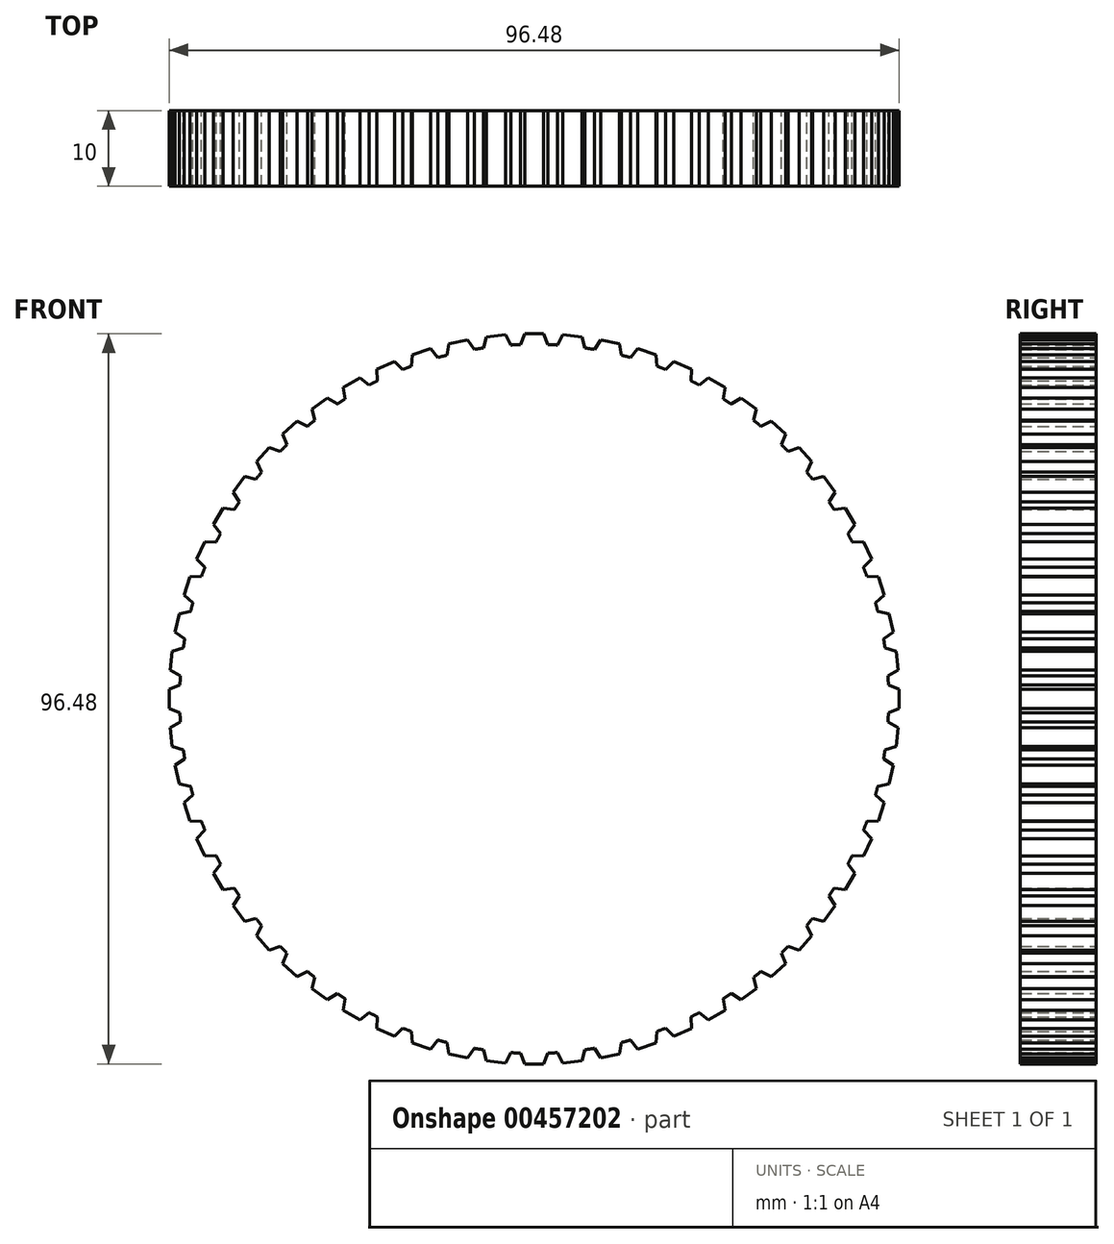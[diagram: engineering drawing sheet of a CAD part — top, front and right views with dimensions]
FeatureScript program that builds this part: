
annotation { "Feature Type Name" : "Feature", "Feature Type Description" : "" }
export const myFeature = defineFeature(function(context is Context, id is Id, definition is map)
    precondition{}
    {
        {
            var Q0;
            Q0=qCreatedBy(makeId("Front.planeOp"),FACE);
            var sketch = newSketch(context, id + "F0", { "sketchPlane" : qUnion([Q0])});
            skCircle(sketch, "E0", {"center": v(0, 0) * mm, "radius": 48.26 * mm, "construction": true});
            skLineSegment(sketch, "E1", {"start": v(0, 48.26) * mm, "end": v(0, 46.86) * mm, "construction": true});
            skCircle(sketch, "E2", {"center": v(0, 0) * mm, "radius": 46.86 * mm});
            skLineSegment(sketch, "E3", {"start": v(0, 0) * mm, "end": v(-1.26, 48.24) * mm, "construction": true});
            skLineSegment(sketch, "E4", {"start": v(0, 0) * mm, "end": v(-2.53, 48.19) * mm, "construction": true});
            skLineSegment(sketch, "E5.MirrorCS", {"start": v(0, 0) * mm, "end": v(1.26, 48.24) * mm, "construction": true});
            skLineSegment(sketch, "E6.MirrorCS", {"start": v(0, 0) * mm, "end": v(2.53, 48.19) * mm, "construction": true});
            skLineSegment(sketch, "E7", {"start": v(-1.26, 48.24) * mm, "end": v(1.26, 48.24) * mm});
            skLineSegment(sketch, "E8", {"start": v(-1.26, 48.24) * mm, "end": v(-1.84, 46.82) * mm});
            skLineSegment(sketch, "E9.MirrorCS", {"start": v(1.26, 48.24) * mm, "end": v(1.84, 46.82) * mm});
            skLineSegment(sketch, "E10.1.0", {"start": v(-6.3, 47.84) * mm, "end": v(-6.72, 46.37) * mm});
            skLineSegment(sketch, "E10.1.1", {"start": v(-6.3, 47.84) * mm, "end": v(-3.79, 48.1) * mm});
            skLineSegment(sketch, "E10.1.2", {"start": v(-3.79, 48.1) * mm, "end": v(-3.07, 46.75) * mm});
            skLineSegment(sketch, "E10.2.0", {"start": v(-11.26, 46.92) * mm, "end": v(-11.53, 45.41) * mm});
            skLineSegment(sketch, "E10.2.1", {"start": v(-11.26, 46.92) * mm, "end": v(-8.8, 47.45) * mm});
            skLineSegment(sketch, "E10.2.2", {"start": v(-8.8, 47.45) * mm, "end": v(-7.94, 46.18) * mm});
            skLineSegment(sketch, "E10.3.0", {"start": v(-16.1, 45.49) * mm, "end": v(-16.21, 43.96) * mm});
            skLineSegment(sketch, "E10.3.1", {"start": v(-16.1, 45.49) * mm, "end": v(-13.7, 46.27) * mm});
            skLineSegment(sketch, "E10.3.2", {"start": v(-13.7, 46.27) * mm, "end": v(-12.72, 45.1) * mm});
            skLineSegment(sketch, "E10.4.0", {"start": v(-20.77, 43.55) * mm, "end": v(-20.72, 42.02) * mm});
            skLineSegment(sketch, "E10.4.1", {"start": v(-20.77, 43.55) * mm, "end": v(-18.47, 44.58) * mm});
            skLineSegment(sketch, "E10.4.2", {"start": v(-18.47, 44.58) * mm, "end": v(-17.37, 43.52) * mm});
            skLineSegment(sketch, "E10.5.0", {"start": v(-25.21, 41.14) * mm, "end": v(-25, 39.63) * mm});
            skLineSegment(sketch, "E10.5.1", {"start": v(-25.21, 41.14) * mm, "end": v(-23.03, 42.4) * mm});
            skLineSegment(sketch, "E10.5.2", {"start": v(-23.03, 42.4) * mm, "end": v(-21.82, 41.46) * mm});
            skLineSegment(sketch, "E10.6.0", {"start": v(-29.38, 38.28) * mm, "end": v(-29, 36.8) * mm});
            skLineSegment(sketch, "E10.6.1", {"start": v(-29.38, 38.28) * mm, "end": v(-27.33, 39.77) * mm});
            skLineSegment(sketch, "E10.6.2", {"start": v(-27.33, 39.77) * mm, "end": v(-26.03, 38.96) * mm});
            skLineSegment(sketch, "E10.7.0", {"start": v(-33.22, 35) * mm, "end": v(-32.7, 33.56) * mm});
            skLineSegment(sketch, "E10.7.1", {"start": v(-33.22, 35) * mm, "end": v(-31.34, 36.7) * mm});
            skLineSegment(sketch, "E10.7.2", {"start": v(-31.34, 36.7) * mm, "end": v(-29.96, 36.02) * mm});
            skLineSegment(sketch, "E10.8.0", {"start": v(-36.7, 31.34) * mm, "end": v(-36.02, 29.96) * mm});
            skLineSegment(sketch, "E10.8.1", {"start": v(-36.7, 31.34) * mm, "end": v(-35, 33.22) * mm});
            skLineSegment(sketch, "E10.8.2", {"start": v(-35, 33.22) * mm, "end": v(-33.56, 32.7) * mm});
            skLineSegment(sketch, "E10.9.0", {"start": v(-39.77, 27.33) * mm, "end": v(-38.96, 26.03) * mm});
            skLineSegment(sketch, "E10.9.1", {"start": v(-39.77, 27.33) * mm, "end": v(-38.28, 29.38) * mm});
            skLineSegment(sketch, "E10.9.2", {"start": v(-38.28, 29.38) * mm, "end": v(-36.8, 29) * mm});
            skLineSegment(sketch, "E11", {"start": v(0, 0) * mm, "end": v(0, 48.26) * mm, "construction": true});
            skLineSegment(sketch, "E12.2.10.0", {"start": v(-42.4, 23.03) * mm, "end": v(-41.46, 21.82) * mm});
            skLineSegment(sketch, "E12.3.10.0", {"start": v(-42.4, 23.03) * mm, "end": v(-41.14, 25.21) * mm});
            skLineSegment(sketch, "E12.6.10.0", {"start": v(-41.14, 25.21) * mm, "end": v(-39.63, 25) * mm});
            skLineSegment(sketch, "E12.2.11.0", {"start": v(-44.58, 18.47) * mm, "end": v(-43.52, 17.37) * mm});
            skLineSegment(sketch, "E12.3.11.0", {"start": v(-44.58, 18.47) * mm, "end": v(-43.55, 20.77) * mm});
            skLineSegment(sketch, "E12.6.11.0", {"start": v(-43.55, 20.77) * mm, "end": v(-42.02, 20.72) * mm});
            skLineSegment(sketch, "E12.2.12.0", {"start": v(-46.27, 13.7) * mm, "end": v(-45.1, 12.72) * mm});
            skLineSegment(sketch, "E12.3.12.0", {"start": v(-46.27, 13.7) * mm, "end": v(-45.49, 16.1) * mm});
            skLineSegment(sketch, "E12.6.12.0", {"start": v(-45.49, 16.1) * mm, "end": v(-43.96, 16.21) * mm});
            skLineSegment(sketch, "E12.2.13.0", {"start": v(-47.45, 8.8) * mm, "end": v(-46.18, 7.94) * mm});
            skLineSegment(sketch, "E12.3.13.0", {"start": v(-47.45, 8.8) * mm, "end": v(-46.92, 11.26) * mm});
            skLineSegment(sketch, "E12.6.13.0", {"start": v(-46.92, 11.26) * mm, "end": v(-45.41, 11.53) * mm});
            skLineSegment(sketch, "E12.2.14.0", {"start": v(-48.1, 3.79) * mm, "end": v(-46.75, 3.07) * mm});
            skLineSegment(sketch, "E12.3.14.0", {"start": v(-48.1, 3.79) * mm, "end": v(-47.84, 6.3) * mm});
            skLineSegment(sketch, "E12.6.14.0", {"start": v(-47.84, 6.3) * mm, "end": v(-46.37, 6.72) * mm});
            skLineSegment(sketch, "E12.2.15.0", {"start": v(-48.24, -1.26) * mm, "end": v(-46.82, -1.84) * mm});
            skLineSegment(sketch, "E12.3.15.0", {"start": v(-48.24, -1.26) * mm, "end": v(-48.24, 1.26) * mm});
            skLineSegment(sketch, "E12.6.15.0", {"start": v(-48.24, 1.26) * mm, "end": v(-46.82, 1.84) * mm});
            skLineSegment(sketch, "E12.2.16.0", {"start": v(-47.84, -6.3) * mm, "end": v(-46.37, -6.72) * mm});
            skLineSegment(sketch, "E12.3.16.0", {"start": v(-47.84, -6.3) * mm, "end": v(-48.1, -3.79) * mm});
            skLineSegment(sketch, "E12.6.16.0", {"start": v(-48.1, -3.79) * mm, "end": v(-46.75, -3.07) * mm});
            skLineSegment(sketch, "E12.2.17.0", {"start": v(-46.92, -11.26) * mm, "end": v(-45.41, -11.53) * mm});
            skLineSegment(sketch, "E12.3.17.0", {"start": v(-46.92, -11.26) * mm, "end": v(-47.45, -8.8) * mm});
            skLineSegment(sketch, "E12.6.17.0", {"start": v(-47.45, -8.8) * mm, "end": v(-46.18, -7.94) * mm});
            skLineSegment(sketch, "E12.2.18.0", {"start": v(-45.49, -16.1) * mm, "end": v(-43.96, -16.21) * mm});
            skLineSegment(sketch, "E12.3.18.0", {"start": v(-45.49, -16.1) * mm, "end": v(-46.27, -13.7) * mm});
            skLineSegment(sketch, "E12.6.18.0", {"start": v(-46.27, -13.7) * mm, "end": v(-45.1, -12.72) * mm});
            skLineSegment(sketch, "E12.2.19.0", {"start": v(-43.55, -20.77) * mm, "end": v(-42.02, -20.72) * mm});
            skLineSegment(sketch, "E12.3.19.0", {"start": v(-43.55, -20.77) * mm, "end": v(-44.58, -18.47) * mm});
            skLineSegment(sketch, "E12.6.19.0", {"start": v(-44.58, -18.47) * mm, "end": v(-43.52, -17.37) * mm});
            skLineSegment(sketch, "E12.2.20.0", {"start": v(-41.14, -25.21) * mm, "end": v(-39.63, -25) * mm});
            skLineSegment(sketch, "E12.3.20.0", {"start": v(-41.14, -25.21) * mm, "end": v(-42.4, -23.03) * mm});
            skLineSegment(sketch, "E12.6.20.0", {"start": v(-42.4, -23.03) * mm, "end": v(-41.46, -21.82) * mm});
            skLineSegment(sketch, "E12.2.21.0", {"start": v(-38.28, -29.38) * mm, "end": v(-36.8, -29) * mm});
            skLineSegment(sketch, "E12.3.21.0", {"start": v(-38.28, -29.38) * mm, "end": v(-39.77, -27.33) * mm});
            skLineSegment(sketch, "E12.6.21.0", {"start": v(-39.77, -27.33) * mm, "end": v(-38.96, -26.03) * mm});
            skLineSegment(sketch, "E12.2.22.0", {"start": v(-35, -33.22) * mm, "end": v(-33.56, -32.7) * mm});
            skLineSegment(sketch, "E12.3.22.0", {"start": v(-35, -33.22) * mm, "end": v(-36.7, -31.34) * mm});
            skLineSegment(sketch, "E12.6.22.0", {"start": v(-36.7, -31.34) * mm, "end": v(-36.02, -29.96) * mm});
            skLineSegment(sketch, "E12.2.23.0", {"start": v(-31.34, -36.7) * mm, "end": v(-29.96, -36.02) * mm});
            skLineSegment(sketch, "E12.3.23.0", {"start": v(-31.34, -36.7) * mm, "end": v(-33.22, -35) * mm});
            skLineSegment(sketch, "E12.6.23.0", {"start": v(-33.22, -35) * mm, "end": v(-32.7, -33.56) * mm});
            skLineSegment(sketch, "E12.2.24.0", {"start": v(-27.33, -39.77) * mm, "end": v(-26.03, -38.96) * mm});
            skLineSegment(sketch, "E12.3.24.0", {"start": v(-27.33, -39.77) * mm, "end": v(-29.38, -38.28) * mm});
            skLineSegment(sketch, "E12.6.24.0", {"start": v(-29.38, -38.28) * mm, "end": v(-29, -36.8) * mm});
            skLineSegment(sketch, "E12.2.25.0", {"start": v(-23.03, -42.4) * mm, "end": v(-21.82, -41.46) * mm});
            skLineSegment(sketch, "E12.3.25.0", {"start": v(-23.03, -42.4) * mm, "end": v(-25.21, -41.14) * mm});
            skLineSegment(sketch, "E12.6.25.0", {"start": v(-25.21, -41.14) * mm, "end": v(-25, -39.63) * mm});
            skLineSegment(sketch, "E12.2.26.0", {"start": v(-18.47, -44.58) * mm, "end": v(-17.37, -43.52) * mm});
            skLineSegment(sketch, "E12.3.26.0", {"start": v(-18.47, -44.58) * mm, "end": v(-20.77, -43.55) * mm});
            skLineSegment(sketch, "E12.6.26.0", {"start": v(-20.77, -43.55) * mm, "end": v(-20.72, -42.02) * mm});
            skLineSegment(sketch, "E12.2.27.0", {"start": v(-13.7, -46.27) * mm, "end": v(-12.72, -45.1) * mm});
            skLineSegment(sketch, "E12.3.27.0", {"start": v(-13.7, -46.27) * mm, "end": v(-16.1, -45.49) * mm});
            skLineSegment(sketch, "E12.6.27.0", {"start": v(-16.1, -45.49) * mm, "end": v(-16.21, -43.96) * mm});
            skLineSegment(sketch, "E12.2.28.0", {"start": v(-8.8, -47.45) * mm, "end": v(-7.94, -46.18) * mm});
            skLineSegment(sketch, "E12.3.28.0", {"start": v(-8.8, -47.45) * mm, "end": v(-11.26, -46.92) * mm});
            skLineSegment(sketch, "E12.6.28.0", {"start": v(-11.26, -46.92) * mm, "end": v(-11.53, -45.41) * mm});
            skLineSegment(sketch, "E12.2.29.0", {"start": v(-3.79, -48.1) * mm, "end": v(-3.07, -46.75) * mm});
            skLineSegment(sketch, "E12.3.29.0", {"start": v(-3.79, -48.1) * mm, "end": v(-6.3, -47.84) * mm});
            skLineSegment(sketch, "E12.6.29.0", {"start": v(-6.3, -47.84) * mm, "end": v(-6.72, -46.37) * mm});
            skLineSegment(sketch, "E12.2.30.0", {"start": v(1.26, -48.24) * mm, "end": v(1.84, -46.82) * mm});
            skLineSegment(sketch, "E12.3.30.0", {"start": v(1.26, -48.24) * mm, "end": v(-1.26, -48.24) * mm});
            skLineSegment(sketch, "E12.6.30.0", {"start": v(-1.26, -48.24) * mm, "end": v(-1.84, -46.82) * mm});
            skLineSegment(sketch, "E12.2.31.0", {"start": v(6.3, -47.84) * mm, "end": v(6.72, -46.37) * mm});
            skLineSegment(sketch, "E12.3.31.0", {"start": v(6.3, -47.84) * mm, "end": v(3.79, -48.1) * mm});
            skLineSegment(sketch, "E12.6.31.0", {"start": v(3.79, -48.1) * mm, "end": v(3.07, -46.75) * mm});
            skLineSegment(sketch, "E12.2.32.0", {"start": v(11.26, -46.92) * mm, "end": v(11.53, -45.41) * mm});
            skLineSegment(sketch, "E12.3.32.0", {"start": v(11.26, -46.92) * mm, "end": v(8.8, -47.45) * mm});
            skLineSegment(sketch, "E12.6.32.0", {"start": v(8.8, -47.45) * mm, "end": v(7.94, -46.18) * mm});
            skLineSegment(sketch, "E12.2.33.0", {"start": v(16.1, -45.49) * mm, "end": v(16.21, -43.96) * mm});
            skLineSegment(sketch, "E12.3.33.0", {"start": v(16.1, -45.49) * mm, "end": v(13.7, -46.27) * mm});
            skLineSegment(sketch, "E12.6.33.0", {"start": v(13.7, -46.27) * mm, "end": v(12.72, -45.1) * mm});
            skLineSegment(sketch, "E12.2.34.0", {"start": v(20.77, -43.55) * mm, "end": v(20.72, -42.02) * mm});
            skLineSegment(sketch, "E12.3.34.0", {"start": v(20.77, -43.55) * mm, "end": v(18.47, -44.58) * mm});
            skLineSegment(sketch, "E12.6.34.0", {"start": v(18.47, -44.58) * mm, "end": v(17.37, -43.52) * mm});
            skLineSegment(sketch, "E12.2.35.0", {"start": v(25.21, -41.14) * mm, "end": v(25, -39.63) * mm});
            skLineSegment(sketch, "E12.3.35.0", {"start": v(25.21, -41.14) * mm, "end": v(23.03, -42.4) * mm});
            skLineSegment(sketch, "E12.6.35.0", {"start": v(23.03, -42.4) * mm, "end": v(21.82, -41.46) * mm});
            skLineSegment(sketch, "E12.2.36.0", {"start": v(29.38, -38.28) * mm, "end": v(29, -36.8) * mm});
            skLineSegment(sketch, "E12.3.36.0", {"start": v(29.38, -38.28) * mm, "end": v(27.33, -39.77) * mm});
            skLineSegment(sketch, "E12.6.36.0", {"start": v(27.33, -39.77) * mm, "end": v(26.03, -38.96) * mm});
            skLineSegment(sketch, "E12.2.37.0", {"start": v(33.22, -35) * mm, "end": v(32.7, -33.56) * mm});
            skLineSegment(sketch, "E12.3.37.0", {"start": v(33.22, -35) * mm, "end": v(31.34, -36.7) * mm});
            skLineSegment(sketch, "E12.6.37.0", {"start": v(31.34, -36.7) * mm, "end": v(29.96, -36.02) * mm});
            skLineSegment(sketch, "E12.2.38.0", {"start": v(36.7, -31.34) * mm, "end": v(36.02, -29.96) * mm});
            skLineSegment(sketch, "E12.3.38.0", {"start": v(36.7, -31.34) * mm, "end": v(35, -33.22) * mm});
            skLineSegment(sketch, "E12.6.38.0", {"start": v(35, -33.22) * mm, "end": v(33.56, -32.7) * mm});
            skLineSegment(sketch, "E12.2.39.0", {"start": v(39.77, -27.33) * mm, "end": v(38.96, -26.03) * mm});
            skLineSegment(sketch, "E12.3.39.0", {"start": v(39.77, -27.33) * mm, "end": v(38.28, -29.38) * mm});
            skLineSegment(sketch, "E12.6.39.0", {"start": v(38.28, -29.38) * mm, "end": v(36.8, -29) * mm});
            skLineSegment(sketch, "E12.2.40.0", {"start": v(42.4, -23.03) * mm, "end": v(41.46, -21.82) * mm});
            skLineSegment(sketch, "E12.3.40.0", {"start": v(42.4, -23.03) * mm, "end": v(41.14, -25.21) * mm});
            skLineSegment(sketch, "E12.6.40.0", {"start": v(41.14, -25.21) * mm, "end": v(39.63, -25) * mm});
            skLineSegment(sketch, "E12.2.41.0", {"start": v(44.58, -18.47) * mm, "end": v(43.52, -17.37) * mm});
            skLineSegment(sketch, "E12.3.41.0", {"start": v(44.58, -18.47) * mm, "end": v(43.55, -20.77) * mm});
            skLineSegment(sketch, "E12.6.41.0", {"start": v(43.55, -20.77) * mm, "end": v(42.02, -20.72) * mm});
            skLineSegment(sketch, "E12.2.42.0", {"start": v(46.27, -13.7) * mm, "end": v(45.1, -12.72) * mm});
            skLineSegment(sketch, "E12.3.42.0", {"start": v(46.27, -13.7) * mm, "end": v(45.49, -16.1) * mm});
            skLineSegment(sketch, "E12.6.42.0", {"start": v(45.49, -16.1) * mm, "end": v(43.96, -16.21) * mm});
            skLineSegment(sketch, "E12.2.43.0", {"start": v(47.45, -8.8) * mm, "end": v(46.18, -7.94) * mm});
            skLineSegment(sketch, "E12.3.43.0", {"start": v(47.45, -8.8) * mm, "end": v(46.92, -11.26) * mm});
            skLineSegment(sketch, "E12.6.43.0", {"start": v(46.92, -11.26) * mm, "end": v(45.41, -11.53) * mm});
            skLineSegment(sketch, "E12.2.44.0", {"start": v(48.1, -3.79) * mm, "end": v(46.75, -3.07) * mm});
            skLineSegment(sketch, "E12.3.44.0", {"start": v(48.1, -3.79) * mm, "end": v(47.84, -6.3) * mm});
            skLineSegment(sketch, "E12.6.44.0", {"start": v(47.84, -6.3) * mm, "end": v(46.37, -6.72) * mm});
            skLineSegment(sketch, "E12.2.45.0", {"start": v(48.24, 1.26) * mm, "end": v(46.82, 1.84) * mm});
            skLineSegment(sketch, "E12.3.45.0", {"start": v(48.24, 1.26) * mm, "end": v(48.24, -1.26) * mm});
            skLineSegment(sketch, "E12.6.45.0", {"start": v(48.24, -1.26) * mm, "end": v(46.82, -1.84) * mm});
            skLineSegment(sketch, "E12.2.46.0", {"start": v(47.84, 6.3) * mm, "end": v(46.37, 6.72) * mm});
            skLineSegment(sketch, "E12.3.46.0", {"start": v(47.84, 6.3) * mm, "end": v(48.1, 3.79) * mm});
            skLineSegment(sketch, "E12.6.46.0", {"start": v(48.1, 3.79) * mm, "end": v(46.75, 3.07) * mm});
            skLineSegment(sketch, "E12.2.47.0", {"start": v(46.92, 11.26) * mm, "end": v(45.41, 11.53) * mm});
            skLineSegment(sketch, "E12.3.47.0", {"start": v(46.92, 11.26) * mm, "end": v(47.45, 8.8) * mm});
            skLineSegment(sketch, "E12.6.47.0", {"start": v(47.45, 8.8) * mm, "end": v(46.18, 7.94) * mm});
            skLineSegment(sketch, "E12.2.48.0", {"start": v(45.49, 16.1) * mm, "end": v(43.96, 16.21) * mm});
            skLineSegment(sketch, "E12.3.48.0", {"start": v(45.49, 16.1) * mm, "end": v(46.27, 13.7) * mm});
            skLineSegment(sketch, "E12.6.48.0", {"start": v(46.27, 13.7) * mm, "end": v(45.1, 12.72) * mm});
            skLineSegment(sketch, "E12.2.49.0", {"start": v(43.55, 20.77) * mm, "end": v(42.02, 20.72) * mm});
            skLineSegment(sketch, "E12.3.49.0", {"start": v(43.55, 20.77) * mm, "end": v(44.58, 18.47) * mm});
            skLineSegment(sketch, "E12.6.49.0", {"start": v(44.58, 18.47) * mm, "end": v(43.52, 17.37) * mm});
            skLineSegment(sketch, "E12.2.50.0", {"start": v(41.14, 25.21) * mm, "end": v(39.63, 25) * mm});
            skLineSegment(sketch, "E12.3.50.0", {"start": v(41.14, 25.21) * mm, "end": v(42.4, 23.03) * mm});
            skLineSegment(sketch, "E12.6.50.0", {"start": v(42.4, 23.03) * mm, "end": v(41.46, 21.82) * mm});
            skLineSegment(sketch, "E12.2.51.0", {"start": v(38.28, 29.38) * mm, "end": v(36.8, 29) * mm});
            skLineSegment(sketch, "E12.3.51.0", {"start": v(38.28, 29.38) * mm, "end": v(39.77, 27.33) * mm});
            skLineSegment(sketch, "E12.6.51.0", {"start": v(39.77, 27.33) * mm, "end": v(38.96, 26.03) * mm});
            skLineSegment(sketch, "E12.2.52.0", {"start": v(35, 33.22) * mm, "end": v(33.56, 32.7) * mm});
            skLineSegment(sketch, "E12.3.52.0", {"start": v(35, 33.22) * mm, "end": v(36.7, 31.34) * mm});
            skLineSegment(sketch, "E12.6.52.0", {"start": v(36.7, 31.34) * mm, "end": v(36.02, 29.96) * mm});
            skLineSegment(sketch, "E12.2.53.0", {"start": v(31.34, 36.7) * mm, "end": v(29.96, 36.02) * mm});
            skLineSegment(sketch, "E12.3.53.0", {"start": v(31.34, 36.7) * mm, "end": v(33.22, 35) * mm});
            skLineSegment(sketch, "E12.6.53.0", {"start": v(33.22, 35) * mm, "end": v(32.7, 33.56) * mm});
            skLineSegment(sketch, "E12.2.54.0", {"start": v(27.33, 39.77) * mm, "end": v(26.03, 38.96) * mm});
            skLineSegment(sketch, "E12.3.54.0", {"start": v(27.33, 39.77) * mm, "end": v(29.38, 38.28) * mm});
            skLineSegment(sketch, "E12.6.54.0", {"start": v(29.38, 38.28) * mm, "end": v(29, 36.8) * mm});
            skLineSegment(sketch, "E12.2.55.0", {"start": v(23.03, 42.4) * mm, "end": v(21.82, 41.46) * mm});
            skLineSegment(sketch, "E12.3.55.0", {"start": v(23.03, 42.4) * mm, "end": v(25.21, 41.14) * mm});
            skLineSegment(sketch, "E12.6.55.0", {"start": v(25.21, 41.14) * mm, "end": v(25, 39.63) * mm});
            skLineSegment(sketch, "E12.2.56.0", {"start": v(18.47, 44.58) * mm, "end": v(17.37, 43.52) * mm});
            skLineSegment(sketch, "E12.3.56.0", {"start": v(18.47, 44.58) * mm, "end": v(20.77, 43.55) * mm});
            skLineSegment(sketch, "E12.6.56.0", {"start": v(20.77, 43.55) * mm, "end": v(20.72, 42.02) * mm});
            skLineSegment(sketch, "E12.2.57.0", {"start": v(13.7, 46.27) * mm, "end": v(12.72, 45.1) * mm});
            skLineSegment(sketch, "E12.3.57.0", {"start": v(13.7, 46.27) * mm, "end": v(16.1, 45.49) * mm});
            skLineSegment(sketch, "E12.6.57.0", {"start": v(16.1, 45.49) * mm, "end": v(16.21, 43.96) * mm});
            skLineSegment(sketch, "E12.2.58.0", {"start": v(8.8, 47.45) * mm, "end": v(7.94, 46.18) * mm});
            skLineSegment(sketch, "E12.3.58.0", {"start": v(8.8, 47.45) * mm, "end": v(11.26, 46.92) * mm});
            skLineSegment(sketch, "E12.6.58.0", {"start": v(11.26, 46.92) * mm, "end": v(11.53, 45.41) * mm});
            skLineSegment(sketch, "E12.2.59.0", {"start": v(3.79, 48.1) * mm, "end": v(3.07, 46.75) * mm});
            skLineSegment(sketch, "E12.3.59.0", {"start": v(3.79, 48.1) * mm, "end": v(6.3, 47.84) * mm});
            skLineSegment(sketch, "E12.6.59.0", {"start": v(6.3, 47.84) * mm, "end": v(6.72, 46.37) * mm});
            skSolve(sketch);
        }
        {
            var Q0;
            Q0 = qSketchRegion(id + "F0", true);
            extrude(context, id + "F1", {"entities" : qUnion([Q0]), "depth" : 10 * mm});
        }
    });
